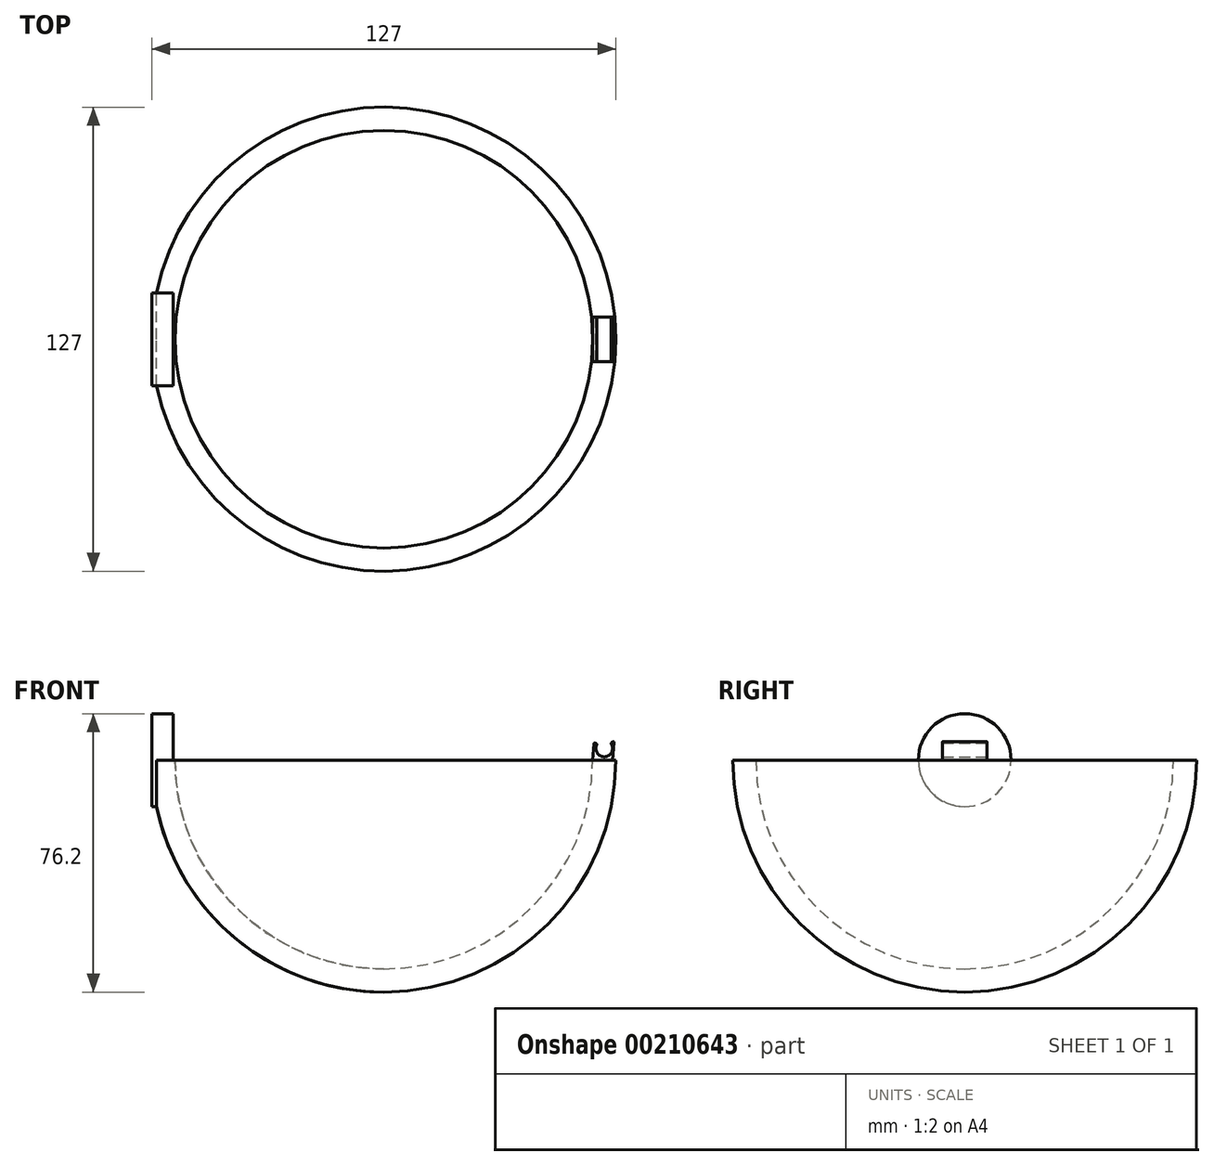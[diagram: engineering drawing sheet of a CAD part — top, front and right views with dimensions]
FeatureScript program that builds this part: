
annotation { "Feature Type Name" : "Feature", "Feature Type Description" : "" }
export const myFeature = defineFeature(function(context is Context, id is Id, definition is map)
    precondition{}
    {
        {
            var Q0;
            Q0=qCreatedBy(makeId("Front.planeOp"),FACE);
            var sketch = newSketch(context, id + "F0", { "sketchPlane" : qUnion([Q0])});
            skLineSegment(sketch, "E0", {"start": v(-63.5, 0) * mm, "end": v(-57.15, 0) * mm});
            skLineSegment(sketch, "E1.MirrorCS", {"start": v(0, -57.15) * mm, "end": v(0, -63.5) * mm});
            skArc(sketch, "E2.MirrorCS", {"start": v(0, -57.15) * mm, "mid": v(-40.41, -40.41) * mm, "end": v(-57.15, 0) * mm});
            skArc(sketch, "E3.MirrorCS", {"start": v(0, -63.5) * mm, "mid": v(-44.9, -44.9) * mm, "end": v(-63.5, 0) * mm});
            skSolve(sketch);
        }
        {
            var Q0;
            Q0=makeQuery(id+"F0.imprint","IMPRINT",FACE,{"disambiguationData":[TD([[makeQuery(id+"F0.imprint","IMPRINT",EDGE,{"derivedFrom":sQuery(id+"F0.wireOp",EDGE,"E0")}),-1.0]])]});
            var Q1;
            Q1=sQuery(id+"F0.wireOp",EDGE,"E1.MirrorCS");
            revolve(context, id + "F1", {"entities" : qUnion([Q0]), "axis" : qUnion([Q1]), "revolveType" : RevolveType.FULL});
        }
        {
            var Q0;
            Q0=qCreatedBy(makeId("Front.planeOp"),FACE);
            var sketch = newSketch(context, id + "F2", { "sketchPlane" : qUnion([Q0])});
            skLineSegment(sketch, "E4", {"start": v(62.59, 0) * mm, "end": v(57.15, 0) * mm});
            skArc(sketch, "E5", {"start": v(58.26, 4.15) * mm, "mid": v(60.42, 0.9) * mm, "end": v(62.3, 4.33) * mm});
            skLineSegment(sketch, "E6", {"start": v(57.15, 0) * mm, "end": v(57.57, 4.57) * mm});
            skLineSegment(sketch, "E7", {"start": v(57.78, 4.68) * mm, "end": v(58.15, 4.49) * mm});
            skLineSegment(sketch, "E8", {"start": v(62.47, 4.87) * mm, "end": v(62.8, 5.02) * mm});
            skLineSegment(sketch, "E9", {"start": v(63, 4.87) * mm, "end": v(62.59, 0) * mm});
            skPoint(sketch, "E10.orphan", {"position": v(63.5, 0) * mm});
            skPoint(sketch, "E11.visualSharp", {"position": v(58.37, 4.37) * mm});
            skArc(sketch, "E11.filletArc", {"start": v(58.26, 4.15) * mm, "mid": v(58.27, 4.34) * mm, "end": v(58.15, 4.49) * mm});
            skPoint(sketch, "E12.visualSharp", {"position": v(57.6, 4.78) * mm});
            skArc(sketch, "E12.filletArc", {"start": v(57.78, 4.68) * mm, "mid": v(57.65, 4.68) * mm, "end": v(57.57, 4.57) * mm});
            skPoint(sketch, "E13.visualSharp", {"position": v(62.05, 4.68) * mm});
            skArc(sketch, "E13.filletArc", {"start": v(62.47, 4.87) * mm, "mid": v(62.27, 4.64) * mm, "end": v(62.3, 4.33) * mm});
            skPoint(sketch, "E14.visualSharp", {"position": v(63.02, 5.12) * mm});
            skArc(sketch, "E14.filletArc", {"start": v(63, 4.87) * mm, "mid": v(62.94, 5) * mm, "end": v(62.8, 5.02) * mm});
            skSolve(sketch);
        }
        {
            var Q0;
            Q0=makeQuery(id+"F2.imprint","IMPRINT",FACE,{"disambiguationData":[TD([[makeQuery(id+"F2.imprint","IMPRINT",EDGE,{"derivedFrom":sQuery(id+"F2.wireOp",EDGE,"E4")}),-1.0]])]});
            extrude(context, id + "F3", {"entities" : qUnion([Q0]), "operationType" : NewBodyOperationType.ADD, "endBound" : BoundingType.SYMMETRIC, "depth" : 12.2 * mm});
        }
        {
            var Q0;
            Q0=qCreatedBy(makeId("Right.planeOp"),FACE);
            cPlane(context, id + "F4", {"entities" : qUnion([Q0]), "cplaneType" : CPlaneType.OFFSET, "offset" : 63.5 * mm, "oppositeDirection" : true, "width" : 152.4 * mm, "height" : 152.4 * mm});
        }
        {
            var Q0;
            Q0=qCreatedBy(id+"F4.planeOp",FACE);
            var sketch = newSketch(context, id + "F5", { "sketchPlane" : qUnion([Q0])});
            skCircle(sketch, "E15", {"center": v(0, 0) * mm, "radius": 12.7 * mm});
            skSolve(sketch);
        }
        {
            var Q0;
            Q0=makeQuery(id+"F5.imprint","IMPRINT",FACE,{"disambiguationData":[TD([[makeQuery(id+"F5.imprint","IMPRINT",EDGE,{"derivedFrom":sQuery(id+"F5.wireOp",EDGE,"E15")}),1.0]])]});
            extrude(context, id + "F6", {"entities" : qUnion([Q0]), "operationType" : NewBodyOperationType.ADD, "depth" : 5.84 * mm});
        }
    });
